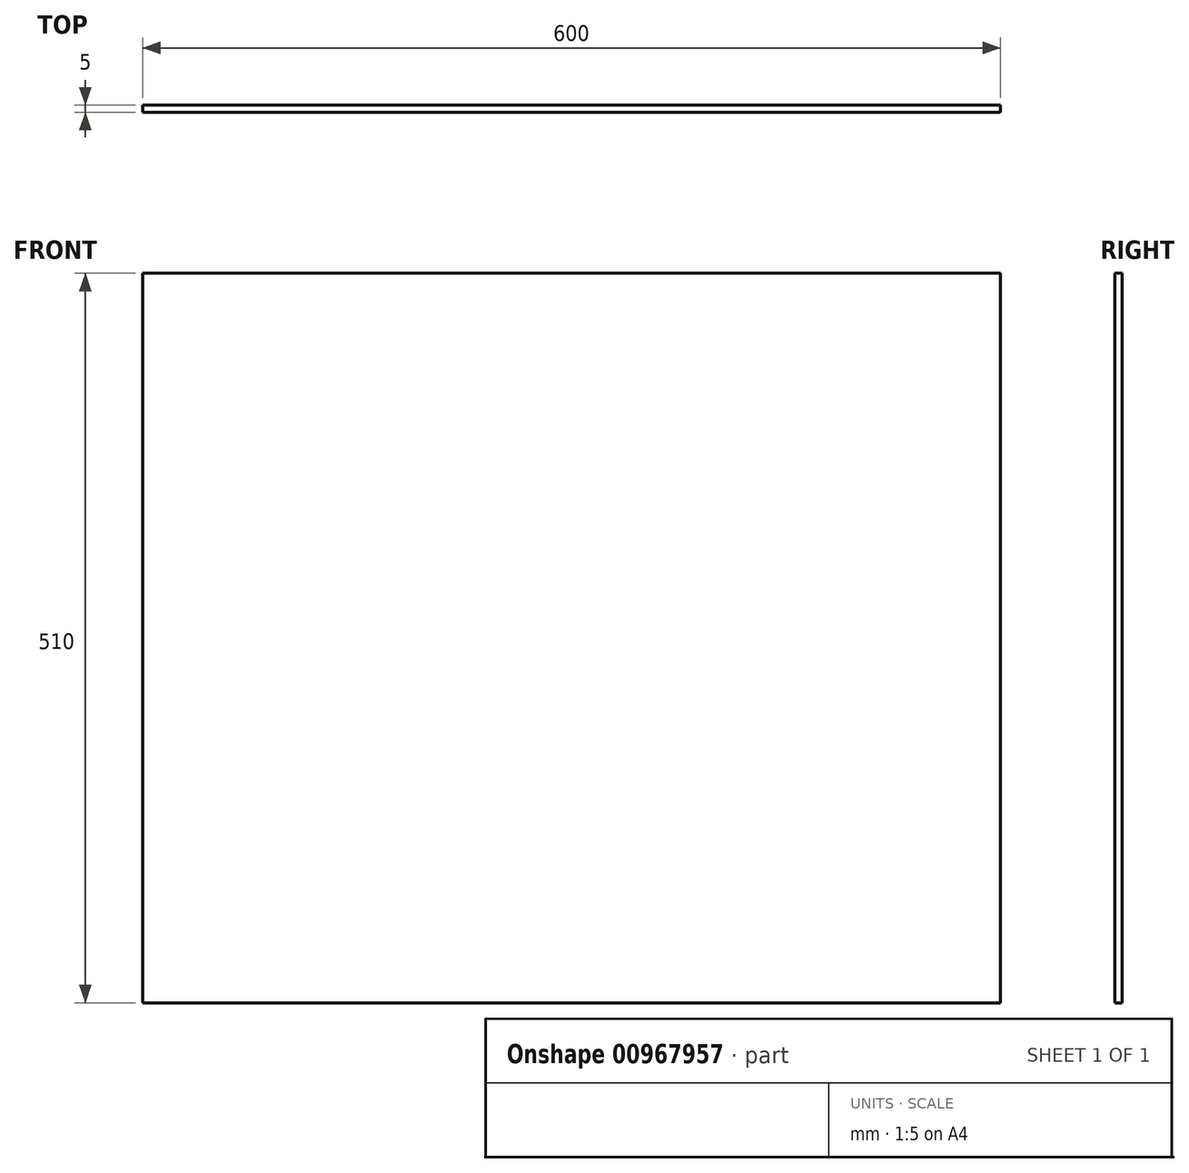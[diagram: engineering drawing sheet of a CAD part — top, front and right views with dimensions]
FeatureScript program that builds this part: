
annotation { "Feature Type Name" : "Feature", "Feature Type Description" : "" }
export const myFeature = defineFeature(function(context is Context, id is Id, definition is map)
    precondition{}
    {
        {
            var Q0;
            Q0=qCreatedBy(makeId("Front.planeOp"),FACE);
            var sketch = newSketch(context, id + "F0", { "sketchPlane" : qUnion([Q0])});
            skLineSegment(sketch, "E0.bottom", {"start": v(300, -255) * mm, "end": v(-300, -255) * mm});
            skLineSegment(sketch, "E0.top", {"start": v(300, 255) * mm, "end": v(-300, 255) * mm});
            skLineSegment(sketch, "E0.left", {"start": v(300, -255) * mm, "end": v(300, 255) * mm});
            skLineSegment(sketch, "E0.right", {"start": v(-300, -255) * mm, "end": v(-300, 255) * mm});
            skPoint(sketch, "E0.middle", {"position": v(0, 0) * mm});
            skSolve(sketch);
        }
        {
            var Q0;
            Q0 = qSketchRegion(id + "F0", true);
            extrude(context, id + "F1", {"entities" : qUnion([Q0]), "depth" : 5 * mm, "offsetDistance" : 25 * mm});
        }
    });
